# Revit family: Shower_Set-Acorn-ShowerWare-538-LVR-DIV-BA-MSH
name_source: partatom
category: Plumbing Fixtures
units: mm (PartAtom-declared; Revit-internal decimal feet)

## family parameters
Cut with Voids When Loaded = No
Host = Face
OmniClass Number = 23.45.05.14.17
OmniClass Title = Showers
Part Type = Normal
Room Calculation Point = No
Round Connector Dimension = Use Diameter
Shared = Yes

## types (2) — shared parameters
0- Electonic Valves, Single-Temp Metering = No
3 - Top or Bottom Supply = Yes
5 - Zenith = Yes
6- Air- Control, Single Temperature Metering = No
A - Anchor Plate = Yes
Adjustable Shower Height = 11"
Assembly Code = D2010710
B - Back Plate, Wall Thickness____ Wall Type____ = No
CSH- Conical Showerhead = No
CW Connection = Yes
CWFU = 3
Cold Water Connection Diameter = 1/2"
D- Soap Dish = No
DIV-FH - Diverter Valve with additional Fixed Head (Shower options specified apply to both shower heads.) = No
DIV-FX - Diverter Valve With Hand Shower & 60" Stainless Steel Hose = No
Default Elevation = 44"
EVS1- Electronic Valve System- Single Temp = No
EVSP1 - Electronic Valve System w/ Piezo Pushbuton = No
F- Flow Control (1.4, 1.6, or 2.0 GPM) = Yes
FX- Hand Shower with 60" Stainless Steel Hose = No
HL - Hi-Lo Mounting Brackets (For Hand Shower) = No
HW Connection = Yes
HWFU = 3
Hot Water Connection Diameter = 1"
Installation Type = Wall Mounted
MV - Metering Valve in Riser (Air-Control) = No
MVC1- Time Trol- Single Temp = No
Manufacturer = Acorn Engineering Company
P- Penal Shower Head = No
PBH- Hemispherical Pushbutton = No
PPZ1 - Programmable Piezo Pushbutton (Single Temperature Only) = No
Product Documentation Link = https://www.acorneng.com
Product Page URL = https://www.acorneng.com
RD- Recessed Soap Dish = No
TF- Transformer = No
Tempered Water Connection Diameter = 1/2"
URL = http://www.acornengineering.com
Vent Connection = No
WFU = 4
WS- Without Showerhead = No
Waste Connection = No
Y- Universal Ball Joint = No
YY- Lockable Universal Ball Joint = No

## per-type parameters (varying)
| type | 8 - T/P Temperature-Pressure Balancing Mixing Valve (ASSE 1016 Compliant) | BA - Bent Arm Head | CI - Cycle Interrupt for Time-Trol Valves | CSH-WSB WaterSense 1.5 GPM Conical Showerhead | Description | Finish | Flow Rate | GR24 24” Glide Rail (For -FX Handheld Shower. Shipped Loose for Wall Mounting) | LVR- Lever Handle (-2, -4 and -5 Valves Only) | MSH- Multi-Stream Shower Head | MTP1 - Single Temp | MTPP1 - Single Temp, Piezo Button | Material |
| 539-F1.4-A | No | No | Yes | Yes | Shower-Ware® Zenith Built-In Showers | Stainless Steel-Acorn-Polished |  | Yes | No | No | Yes | Yes | Metal-Acorn-Stainless Steel-High Polished |
| 538-LVR-DIV-BA-MSH | Yes | Yes | No | No | Zenith Built-In Shower | Brass-Acorn-Stainless Steel | 1.6 GPM | No | Yes | Yes | No | No | Brass-Acorn-Stainless Steel |

note: column(s) folded — value = type name in every type: Model

## geometry (parser evidence)
native form markers: Sweep x9
no freeform markers — native parametric forms only
